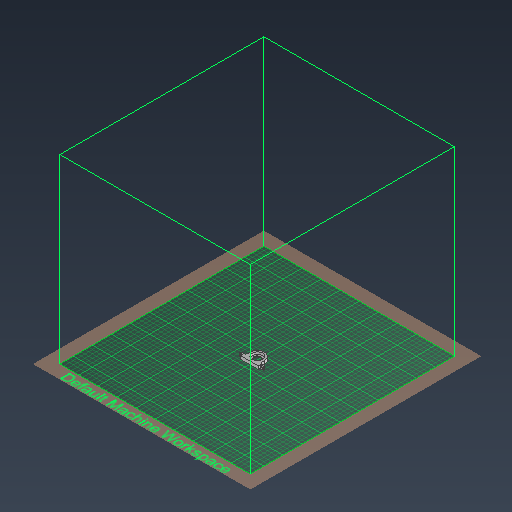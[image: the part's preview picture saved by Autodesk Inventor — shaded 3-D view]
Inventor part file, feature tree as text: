
AUTODESK INVENTOR PART (.ipt)
format: ipt  version: 2021 (Build 250183000, 183)  size: 351,232 bytes
history: native  units: mm
features: extrude x8, sketch x8, fillet x2
ambient origin geometry x8: Origin, YZ Plane, XZ Plane, XY Plane, X Axis, Y Axis, Z Axis, Center Point
bodies: Volumenkörper1 (feature_tree)
feature tree (18):
  extrude  "Extrusion1"  Depth=32.0mm
  sketch  "Skizze2"  dims[d2=24.2mm d3=7.0mm d4=0.0mm d5=6.0mm]
  sketch  "Skizze3"  dims[d6=6.0mm d11=24.2mm]
  extrude  "Extrusion4"  Depth=7.0mm TaperAngle=0.0deg
  fillet  "Rundung1"  Radius=6.0mm
  extrude  "Extrusion6"  Depth=24.2mm
  extrude  "Extrusion7"  Depth=2.0mm TaperAngle=0.0deg
  extrude  "Extrusion8"  Depth=13.0mm TaperAngle=0.0deg
  extrude  "Extrusion9"  Depth=13.0mm
  extrude  "Extrusion10"  Depth=3.5mm
  fillet  "Rundung3"  Radius=3.2mm
  extrude  "Extrusion11"  Depth=3.5mm
  sketch  "Skizze1"  dims[d0=32.0mm d1=32.0mm]
  sketch  "Skizze4"  dims[d12=16.5mm d13=2.0mm d14=0.0mm]
  sketch  "Skizze6"  dims[d15=16.0mm d25=13.0mm d26=0.0mm]
  sketch  "Skizze7"  dims[d27=13.0mm d28=0.0mm d29=3.2mm]
  sketch  "Skizze8"  dims[d30=3.5mm d31=3.5mm d32=3.2mm]
  sketch  "Skizze9"  dims[d33=3.5mm d34=3.5mm d35=10.5mm d36=0.0mm d37=3.5mm d38=0.0mm d39=3.5mm d40=0.0mm d41=3.5mm d42=1.5mm d43=0.0mm]
